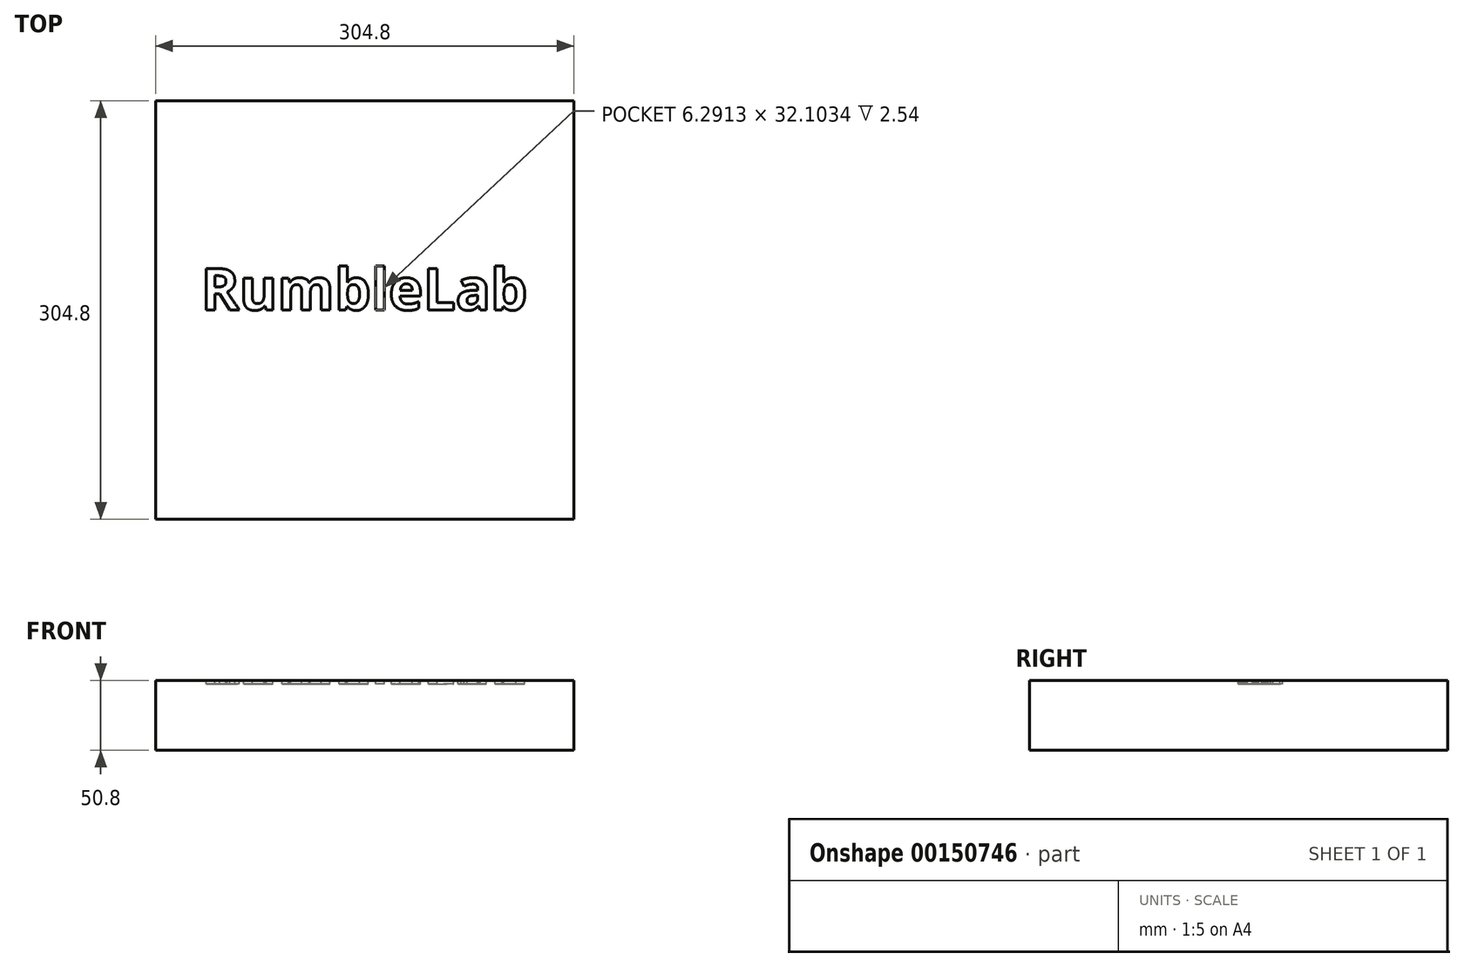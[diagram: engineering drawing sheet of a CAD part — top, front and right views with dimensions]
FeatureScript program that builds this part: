
annotation { "Feature Type Name" : "Feature", "Feature Type Description" : "" }
export const myFeature = defineFeature(function(context is Context, id is Id, definition is map)
    precondition{}
    {
        {
            var Q0;
            Q0=qCreatedBy(makeId("Top.planeOp"),FACE);
            var sketch = newSketch(context, id + "F0", { "sketchPlane" : qUnion([Q0])});
            skLineSegment(sketch, "E0.bottom", {"start": v(-152.4, 152.4) * mm, "end": v(152.4, 152.4) * mm});
            skLineSegment(sketch, "E0.top", {"start": v(-152.4, -152.4) * mm, "end": v(152.4, -152.4) * mm});
            skLineSegment(sketch, "E0.left", {"start": v(-152.4, 152.4) * mm, "end": v(-152.4, -152.4) * mm});
            skLineSegment(sketch, "E0.right", {"start": v(152.4, 152.4) * mm, "end": v(152.4, -152.4) * mm});
            skSolve(sketch);
        }
        {
            var Q0;
            Q0=makeQuery(id+"F0.imprint","IMPRINT",FACE,{"disambiguationData":[TD([[makeQuery(id+"F0.imprint","IMPRINT",EDGE,{"derivedFrom":sQuery(id+"F0.wireOp",EDGE,"E0.bottom")}),-1.0]])]});
            extrude(context, id + "F1", {"entities" : qUnion([Q0]), "depth" : 50.8 * mm});
        }
        {
            var Q0;
            Q0=makeQuery(id+"F1.opExtrude","CAP_FACE",FACE,{"disambiguationData":[OSD([sQuery(id+"F0.wireOp",EDGE,"E0.bottom"),sQuery(id+"F0.wireOp",EDGE,"E0.top"),sQuery(id+"F0.wireOp",EDGE,"E0.left"),sQuery(id+"F0.wireOp",EDGE,"E0.right")])],"isStart":false});
            var sketch = newSketch(context, id + "F2", { "sketchPlane" : qUnion([Q0])});
            skText(sketch, "E1", { "text": "RumbleLab", "fontName": "OpenSans-Bold.ttf"});
            const initialGuessF2  = {"E1": [-0.11935, 0, 1, 0, 0.03042]};
            skSetInitialGuess(sketch, initialGuessF2);
            skSolve(sketch);
        }
        {
            var Q0;
            Q0 = qSketchRegion(id + "F2", true);
            extrude(context, id + "F3", {"entities" : qUnion([Q0]), "operationType" : NewBodyOperationType.REMOVE, "oppositeDirection" : true, "depth" : 2.54 * mm});
        }
    });
